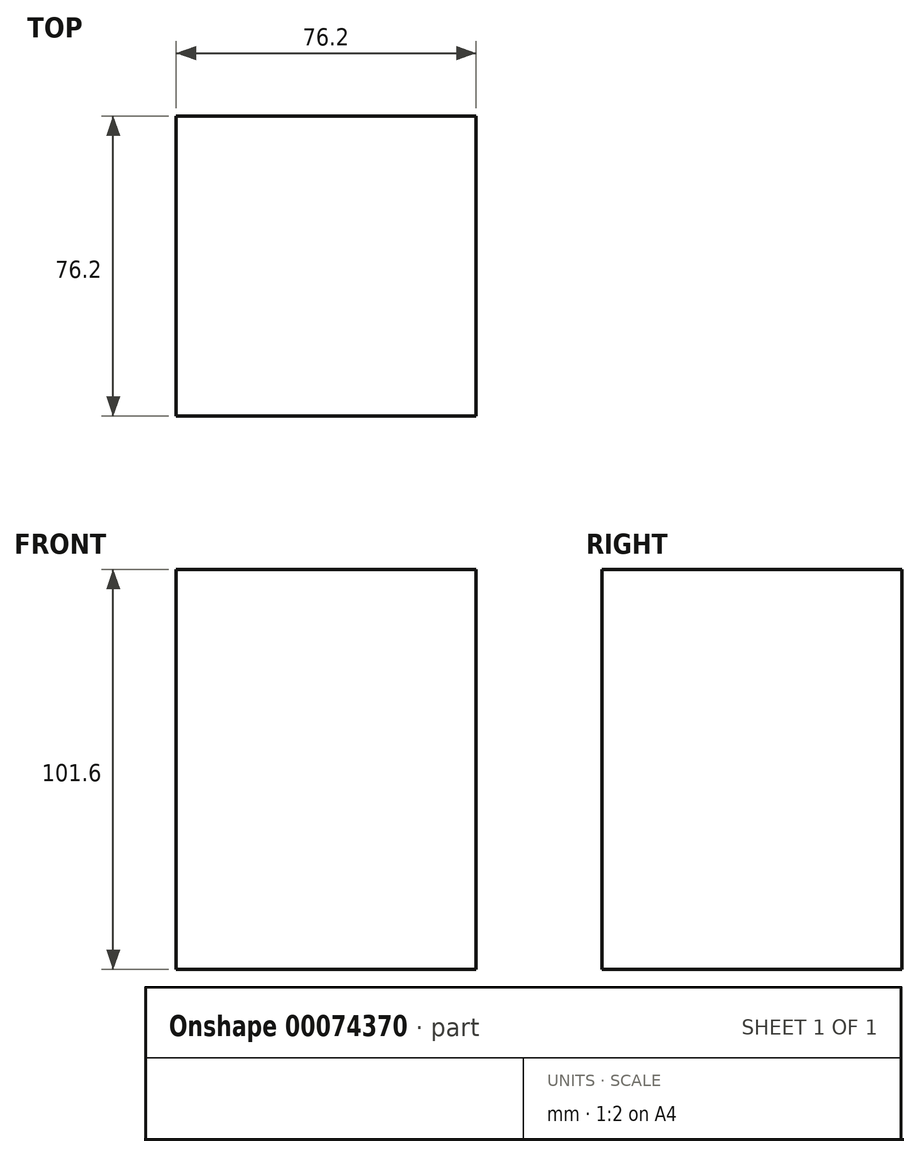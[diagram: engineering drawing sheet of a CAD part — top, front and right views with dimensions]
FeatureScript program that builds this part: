
annotation { "Feature Type Name" : "Feature", "Feature Type Description" : "" }
export const myFeature = defineFeature(function(context is Context, id is Id, definition is map)
    precondition{}
    {
        {
            var Q0;
            Q0=qCreatedBy(makeId("Top.planeOp"),FACE);
            var sketch = newSketch(context, id + "F0", { "sketchPlane" : qUnion([Q0])});
            skLineSegment(sketch, "E0.rect.bottom", {"start": v(38.1, -38.1) * mm, "end": v(-38.1, -38.1) * mm});
            skLineSegment(sketch, "E0.rect.top", {"start": v(38.1, 38.1) * mm, "end": v(-38.1, 38.1) * mm});
            skLineSegment(sketch, "E0.rect.left", {"start": v(38.1, -38.1) * mm, "end": v(38.1, 38.1) * mm});
            skLineSegment(sketch, "E0.rect.right", {"start": v(-38.1, -38.1) * mm, "end": v(-38.1, 38.1) * mm});
            skPoint(sketch, "E0.rect.middle", {"position": v(0, 0) * mm});
            skSolve(sketch);
        }
        {
            var Q0;
            Q0=makeQuery(id+"F0.imprint","IMPRINT",FACE,{"disambiguationData":[TD([[makeQuery(id+"F0.imprint","IMPRINT",EDGE,{"derivedFrom":sQuery(id+"F0.wireOp",EDGE,"E0.rect.bottom")}),-1.0]])]});
            extrude(context, id + "F1", {"entities" : qUnion([Q0]), "endBound" : BoundingType.SYMMETRIC, "depth" : 101.6 * mm});
        }
    });
